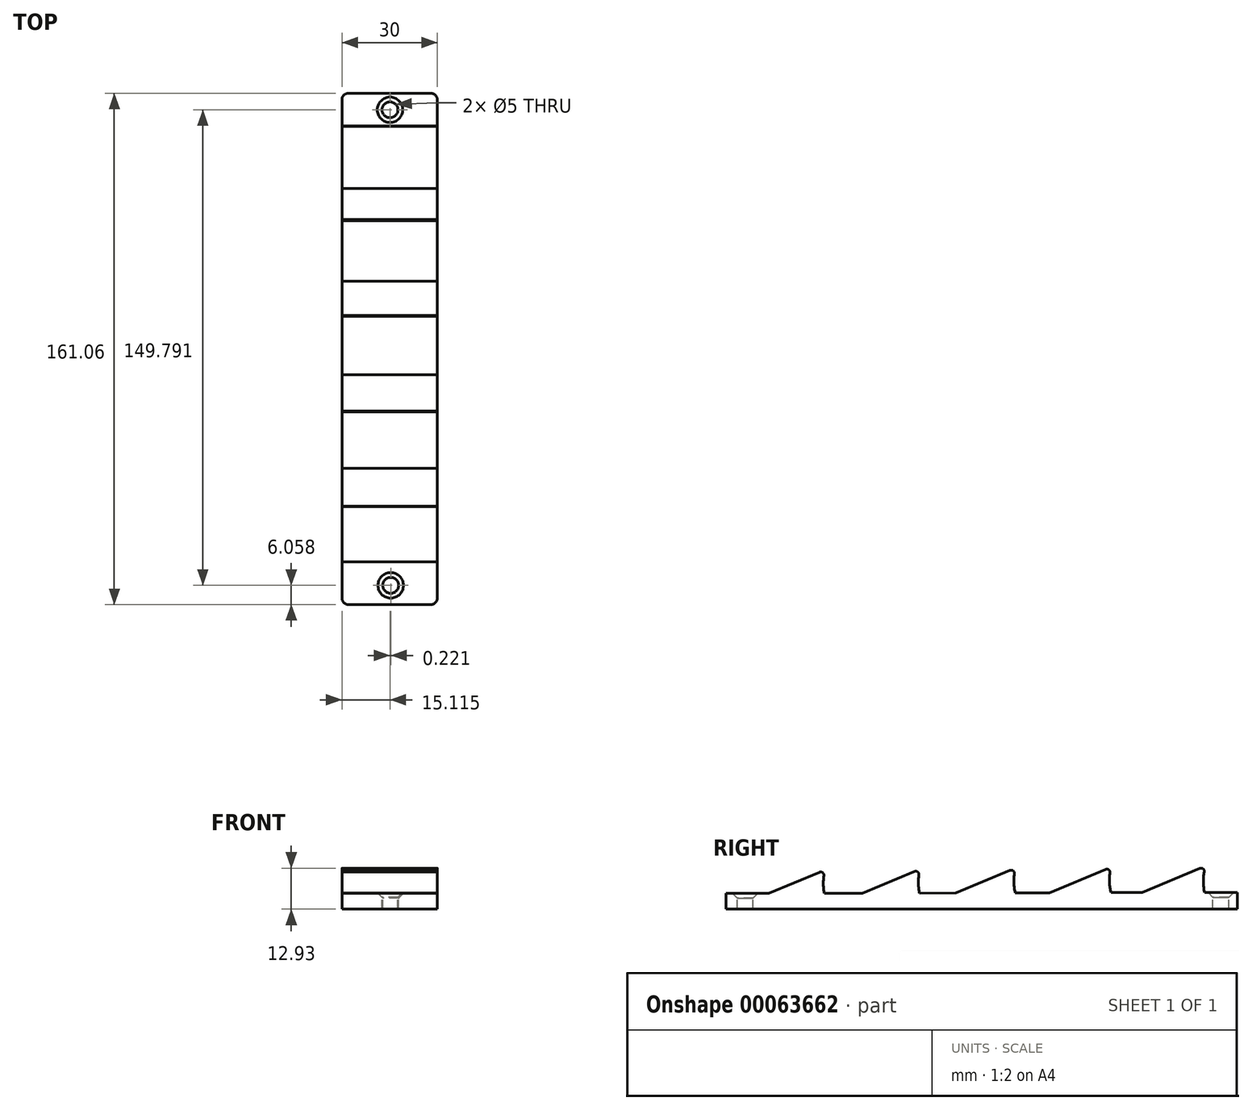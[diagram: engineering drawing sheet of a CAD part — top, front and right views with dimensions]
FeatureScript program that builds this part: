
annotation { "Feature Type Name" : "Feature", "Feature Type Description" : "" }
export const myFeature = defineFeature(function(context is Context, id is Id, definition is map)
    precondition{}
    {
        {
            var Q0;
            Q0=qCreatedBy(makeId("Right.planeOp"),FACE);
            var sketch = newSketch(context, id + "F0", { "sketchPlane" : qUnion([Q0])});
            skLineSegment(sketch, "E0", {"start": v(-103.28, 1.64) * mm, "end": v(36.72, 1.64) * mm});
            skLineSegment(sketch, "E1", {"start": v(-100.86, 6.61) * mm, "end": v(-83.13, 14.02) * mm});
            skArc(sketch, "E2", {"start": v(-83.13, 14.02) * mm, "mid": v(-83.67, 10.33) * mm, "end": v(-83.34, 6.61) * mm});
            skLineSegment(sketch, "E3", {"start": v(-71.4, 6.64) * mm, "end": v(-53.2, 14.24) * mm});
            skArc(sketch, "E4", {"start": v(-53.2, 14.24) * mm, "mid": v(-53.75, 10.48) * mm, "end": v(-53.39, 6.7) * mm});
            skLineSegment(sketch, "E5", {"start": v(-41.93, 6.72) * mm, "end": v(-23.12, 14.58) * mm});
            skArc(sketch, "E6", {"start": v(-23.12, 14.58) * mm, "mid": v(-23.66, 10.68) * mm, "end": v(-23.24, 6.77) * mm});
            skLineSegment(sketch, "E7", {"start": v(-12.46, 6.8) * mm, "end": v(6.97, 14.92) * mm});
            skArc(sketch, "E8", {"start": v(6.97, 14.92) * mm, "mid": v(6.43, 10.9) * mm, "end": v(6.92, 6.86) * mm});
            skLineSegment(sketch, "E9", {"start": v(16.72, 6.88) * mm, "end": v(36.78, 15.26) * mm});
            skArc(sketch, "E10", {"start": v(36.78, 15.26) * mm, "mid": v(36.03, 11.1) * mm, "end": v(36.39, 6.88) * mm});
            skLineSegment(sketch, "E11", {"start": v(36.72, 1.64) * mm, "end": v(46.72, 1.64) * mm});
            skLineSegment(sketch, "E12", {"start": v(46.72, 1.64) * mm, "end": v(46.72, 5.64) * mm});
            skLineSegment(sketch, "E13", {"start": v(6.92, 6.86) * mm, "end": v(16.72, 6.88) * mm});
            skLineSegment(sketch, "E14", {"start": v(16.72, 6.88) * mm, "end": v(6.92, 6.86) * mm});
            skPoint(sketch, "E15.orphan", {"position": v(-13.08, 6.54) * mm});
            skPoint(sketch, "E16.orphan", {"position": v(-23.18, 6.52) * mm});
            skLineSegment(sketch, "E17.trimOffspring", {"start": v(-12.46, 6.8) * mm, "end": v(-23.24, 6.77) * mm});
            skLineSegment(sketch, "E18.trimOffspring", {"start": v(-41.93, 6.72) * mm, "end": v(-53.39, 6.7) * mm});
            skPoint(sketch, "E19.orphan", {"position": v(-53.27, 6.18) * mm});
            skPoint(sketch, "E20.orphan", {"position": v(-43.18, 6.2) * mm});
            skLineSegment(sketch, "E21.trimOffspring", {"start": v(-71.4, 6.64) * mm, "end": v(-83.34, 6.61) * mm});
            skPoint(sketch, "E22.orphan", {"position": v(-73.27, 5.86) * mm});
            skPoint(sketch, "E23.orphan", {"position": v(-83.2, 5.95) * mm});
            skLineSegment(sketch, "E24", {"start": v(36.39, 6.88) * mm, "end": v(46.72, 6.88) * mm});
            skPoint(sketch, "E25.orphan", {"position": v(36.72, 5.64) * mm});
            skLineSegment(sketch, "E26", {"start": v(46.72, 5.64) * mm, "end": v(46.72, 6.88) * mm});
            skLineSegment(sketch, "E27.top", {"start": v(-103.2, 1.64) * mm, "end": v(-103.28, 1.64) * mm});
            skLineSegment(sketch, "E28", {"start": v(-100.86, 6.61) * mm, "end": v(-114.34, 6.61) * mm});
            skLineSegment(sketch, "E29", {"start": v(-114.34, 6.61) * mm, "end": v(-114.34, 1.64) * mm});
            skPoint(sketch, "E27.right.end.orphan", {"position": v(-110.77, 1.64) * mm});
            skPoint(sketch, "E30.orphan", {"position": v(-103.2, 5.64) * mm});
            skLineSegment(sketch, "E31", {"start": v(-103.2, 1.64) * mm, "end": v(-114.34, 1.64) * mm});
            skSolve(sketch);
        }
        {
            var Q0;
            Q0 = qSketchRegion(id + "F0", true);
            var Q1;
            Q1=sQuery(id+"F0.wireOp",EDGE,"E0");
            var Q2;
            Q2=sQuery(id+"F0.wireOp",EDGE,"E1");
            var Q3;
            Q3=sQuery(id+"F0.wireOp",EDGE,"E2");
            var Q4;
            Q4=sQuery(id+"F0.wireOp",EDGE,"aVXR79yY-1hjt-y3u3-m6eV-zaEhtOIxPnFv");
            var Q5;
            Q5=sQuery(id+"F0.wireOp",EDGE,"4554b6e0-54a2-462e-aa4e-58822ef9da20");
            var Q6;
            Q6=sQuery(id+"F0.wireOp",EDGE,"E3");
            var Q7;
            Q7=sQuery(id+"F0.wireOp",EDGE,"E4");
            var Q8;
            Q8=sQuery(id+"F0.wireOp",EDGE,"a5485bb7-b8e9-40f3-8546-a96ed6ddff3a");
            var Q9;
            Q9=sQuery(id+"F0.wireOp",EDGE,"E5");
            var Q10;
            Q10=sQuery(id+"F0.wireOp",EDGE,"E6");
            var Q11;
            Q11=sQuery(id+"F0.wireOp",EDGE,"a28d2f95-e289-46cd-9a1f-94b747a0afc5");
            var Q12;
            Q12=sQuery(id+"F0.wireOp",EDGE,"E7");
            var Q13;
            Q13=sQuery(id+"F0.wireOp",EDGE,"E8");
            var Q14;
            Q14=sQuery(id+"F0.wireOp",EDGE,"E12");
            var Q15;
            Q15=sQuery(id+"F0.wireOp",EDGE,"ae9abd8c-4da3-48e8-ab53-a4a2666a44f8");
            var Q16;
            Q16=sQuery(id+"F0.wireOp",EDGE,"E11");
            var Q17;
            Q17=sQuery(id+"F0.wireOp",EDGE,"E9");
            var Q18;
            Q18=sQuery(id+"F0.wireOp",EDGE,"E10");
            var Q19;
            Q19=sQuery(id+"F0.wireOp",EDGE,"KTlvuNxW-LSAw-ywOI-KxQU-ba1FE6igpGGa");
            extrude(context, id + "F1", {"entities" : qUnion([Q0]), "surfaceEntities" : qUnion([Q1, Q2, Q3, Q4, Q5, Q6, Q7, Q8, Q9, Q10, Q11, Q12, Q13, Q14, Q15, Q16, Q17, Q18, Q19]), "depth" : 30 * mm});
        }
        {
            var Q0;
            Q0=makeQuery(id+"F1.opExtrude","CAP_EDGE",EDGE,{"disambiguationData":[OSD([sQuery(id+"F0.wireOp",EDGE,"E29")])],"isStart":true});
            var Q1;
            Q1=makeQuery(id+"F1.opExtrude","CAP_EDGE",EDGE,{"disambiguationData":[OSD([sQuery(id+"F0.wireOp",EDGE,"E29")])],"isStart":false});
            var Q2;
            Q2=makeQuery(id+"F1.opExtrude","CAP_EDGE",EDGE,{"disambiguationData":[OSD([sQuery(id+"F0.wireOp",EDGE,"E12"),sQuery(id+"F0.wireOp",EDGE,"E26")])],"isStart":true});
            var Q3;
            Q3=makeQuery(id+"F1.opExtrude","CAP_EDGE",EDGE,{"disambiguationData":[OSD([sQuery(id+"F0.wireOp",EDGE,"E12"),sQuery(id+"F0.wireOp",EDGE,"E26")])],"isStart":false});
            fillet(context, id + "F2", {"entities" : qUnion([Q0, Q1, Q2, Q3]), "radius" : 2 * mm, "tangentPropagation" : true, "allowEdgeOverflow" : false});
        }
        {
            var Q0;
            Q0=makeQuery(id+"F1.opExtrude","SWEPT_EDGE",EDGE,{"disambiguationData":[OSD([sQuery(id+"F0.wireOp",EDGE,"E9"),sQuery(id+"F0.wireOp",EDGE,"E10")])]});
            var Q1;
            Q1=makeQuery(id+"F1.opExtrude","SWEPT_EDGE",EDGE,{"disambiguationData":[OSD([sQuery(id+"F0.wireOp",EDGE,"E7"),sQuery(id+"F0.wireOp",EDGE,"E8")])]});
            var Q2;
            Q2=makeQuery(id+"F1.opExtrude","SWEPT_EDGE",EDGE,{"disambiguationData":[OSD([sQuery(id+"F0.wireOp",EDGE,"E5"),sQuery(id+"F0.wireOp",EDGE,"E6")])]});
            var Q3;
            Q3=makeQuery(id+"F1.opExtrude","SWEPT_EDGE",EDGE,{"disambiguationData":[OSD([sQuery(id+"F0.wireOp",EDGE,"E3"),sQuery(id+"F0.wireOp",EDGE,"E4")])]});
            var Q4;
            Q4=makeQuery(id+"F1.opExtrude","SWEPT_EDGE",EDGE,{"disambiguationData":[OSD([sQuery(id+"F0.wireOp",EDGE,"E1"),sQuery(id+"F0.wireOp",EDGE,"E2")])]});
            fillet(context, id + "F3", {"entities" : qUnion([Q0, Q1, Q2, Q3, Q4]), "radius" : 1 * mm, "tangentPropagation" : true, "allowEdgeOverflow" : false});
        }
        {
            var Q0;
            Q0=makeQuery(id+"F1.opExtrude","SWEPT_FACE",FACE,{"disambiguationData":[OSD([sQuery(id+"F0.wireOp",EDGE,"E28")])]});
            var sketch = newSketch(context, id + "F4", { "sketchPlane" : qUnion([Q0])});
            skPoint(sketch, "E32", {"position": v(15.34, -108.28) * mm});
            skPoint(sketch, "E33", {"position": v(161.37, -142.1) * mm});
            skSolve(sketch);
        }
        {
            var Q0;
            Q0=sQuery(id+"F4.wireOp",VERTEX,"E32");
            var Q1;
            Q1=makeQuery(id+"F1.opExtrude","SWEPT_BODY",BODY,{"disambiguationData":[OSD([sQuery(id+"F0.wireOp",EDGE,"E0"),sQuery(id+"F0.wireOp",EDGE,"E1"),sQuery(id+"F0.wireOp",EDGE,"E2"),sQuery(id+"F0.wireOp",EDGE,"E3"),sQuery(id+"F0.wireOp",EDGE,"E4"),sQuery(id+"F0.wireOp",EDGE,"E5"),sQuery(id+"F0.wireOp",EDGE,"E6"),sQuery(id+"F0.wireOp",EDGE,"E7"),sQuery(id+"F0.wireOp",EDGE,"E8"),sQuery(id+"F0.wireOp",EDGE,"E9"),sQuery(id+"F0.wireOp",EDGE,"E10"),sQuery(id+"F0.wireOp",EDGE,"E11"),sQuery(id+"F0.wireOp",EDGE,"E12"),sQuery(id+"F0.wireOp",EDGE,"E14"),sQuery(id+"F0.wireOp",EDGE,"E17.trimOffspring"),sQuery(id+"F0.wireOp",EDGE,"E18.trimOffspring"),sQuery(id+"F0.wireOp",EDGE,"E21.trimOffspring"),sQuery(id+"F0.wireOp",EDGE,"E24"),sQuery(id+"F0.wireOp",EDGE,"E26"),sQuery(id+"F0.wireOp",EDGE,"E28"),sQuery(id+"F0.wireOp",EDGE,"E29"),sQuery(id+"F0.wireOp",EDGE,"E31")])]});
            hole(context, id + "F5", {"style" : HoleStyle.C_SINK, "holeDiameter" : 5 * mm, "cSinkDiameter" : 8 * mm, "endStyle" : HoleEndStyle.THROUGH, "locations" : qUnion([Q0]), "scope" : qUnion([Q1]), "cSinkAngle" : 90 * degree});
        }
        {
            var Q0;
            Q0=makeQuery(id+"F1.opExtrude","SWEPT_FACE",FACE,{"disambiguationData":[OSD([sQuery(id+"F0.wireOp",EDGE,"E24")])]});
            var sketch = newSketch(context, id + "F6", { "sketchPlane" : qUnion([Q0])});
            skPoint(sketch, "E34", {"position": v(15.11, 41.5) * mm});
            skSolve(sketch);
        }
        {
            var Q0;
            Q0=sQuery(id+"F6.wireOp",VERTEX,"E34");
            var Q1;
            Q1=makeQuery(id+"F1.opExtrude","SWEPT_BODY",BODY,{"disambiguationData":[OSD([sQuery(id+"F0.wireOp",EDGE,"E0"),sQuery(id+"F0.wireOp",EDGE,"E1"),sQuery(id+"F0.wireOp",EDGE,"E2"),sQuery(id+"F0.wireOp",EDGE,"E3"),sQuery(id+"F0.wireOp",EDGE,"E4"),sQuery(id+"F0.wireOp",EDGE,"E5"),sQuery(id+"F0.wireOp",EDGE,"E6"),sQuery(id+"F0.wireOp",EDGE,"E7"),sQuery(id+"F0.wireOp",EDGE,"E8"),sQuery(id+"F0.wireOp",EDGE,"E9"),sQuery(id+"F0.wireOp",EDGE,"E10"),sQuery(id+"F0.wireOp",EDGE,"E11"),sQuery(id+"F0.wireOp",EDGE,"E12"),sQuery(id+"F0.wireOp",EDGE,"E14"),sQuery(id+"F0.wireOp",EDGE,"E17.trimOffspring"),sQuery(id+"F0.wireOp",EDGE,"E18.trimOffspring"),sQuery(id+"F0.wireOp",EDGE,"E21.trimOffspring"),sQuery(id+"F0.wireOp",EDGE,"E24"),sQuery(id+"F0.wireOp",EDGE,"E26"),sQuery(id+"F0.wireOp",EDGE,"E28"),sQuery(id+"F0.wireOp",EDGE,"E29"),sQuery(id+"F0.wireOp",EDGE,"E31")])]});
            hole(context, id + "F7", {"style" : HoleStyle.C_SINK, "holeDiameter" : 5 * mm, "cSinkDiameter" : 8 * mm, "endStyle" : HoleEndStyle.THROUGH, "locations" : qUnion([Q0]), "scope" : qUnion([Q1]), "cSinkAngle" : 90 * degree});
        }
    });
